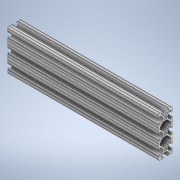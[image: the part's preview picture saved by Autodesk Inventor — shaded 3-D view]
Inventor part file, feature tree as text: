
AUTODESK INVENTOR PART (.ipt)
format: ipt  version: 2020 (Build 240168000, 168)  size: 380,416 bytes
history: native  units: in
note: dims shown in document units (in); Inventor stores cm internally (conversion verified against a paired STEP export)
features: sketch x2, extrude x1
ambient origin geometry x8: Origin, YZ Plane, XZ Plane, XY Plane, X Axis, Y Axis, Z Axis, Center Point
bodies: Solid1 (feature_tree)
feature tree (3):
  extrude  "Extrusion1"  [1 undecoded]
  sketch  "Sketch2"
  sketch  "Sketch1"  dims[d0=11.0in d1=0.0in]
note: 1 required parameter value undecoded (feature->parameter linkage not recoverable at this tier; creation-order binding heuristic only, values carry confidence <= 0.55)
